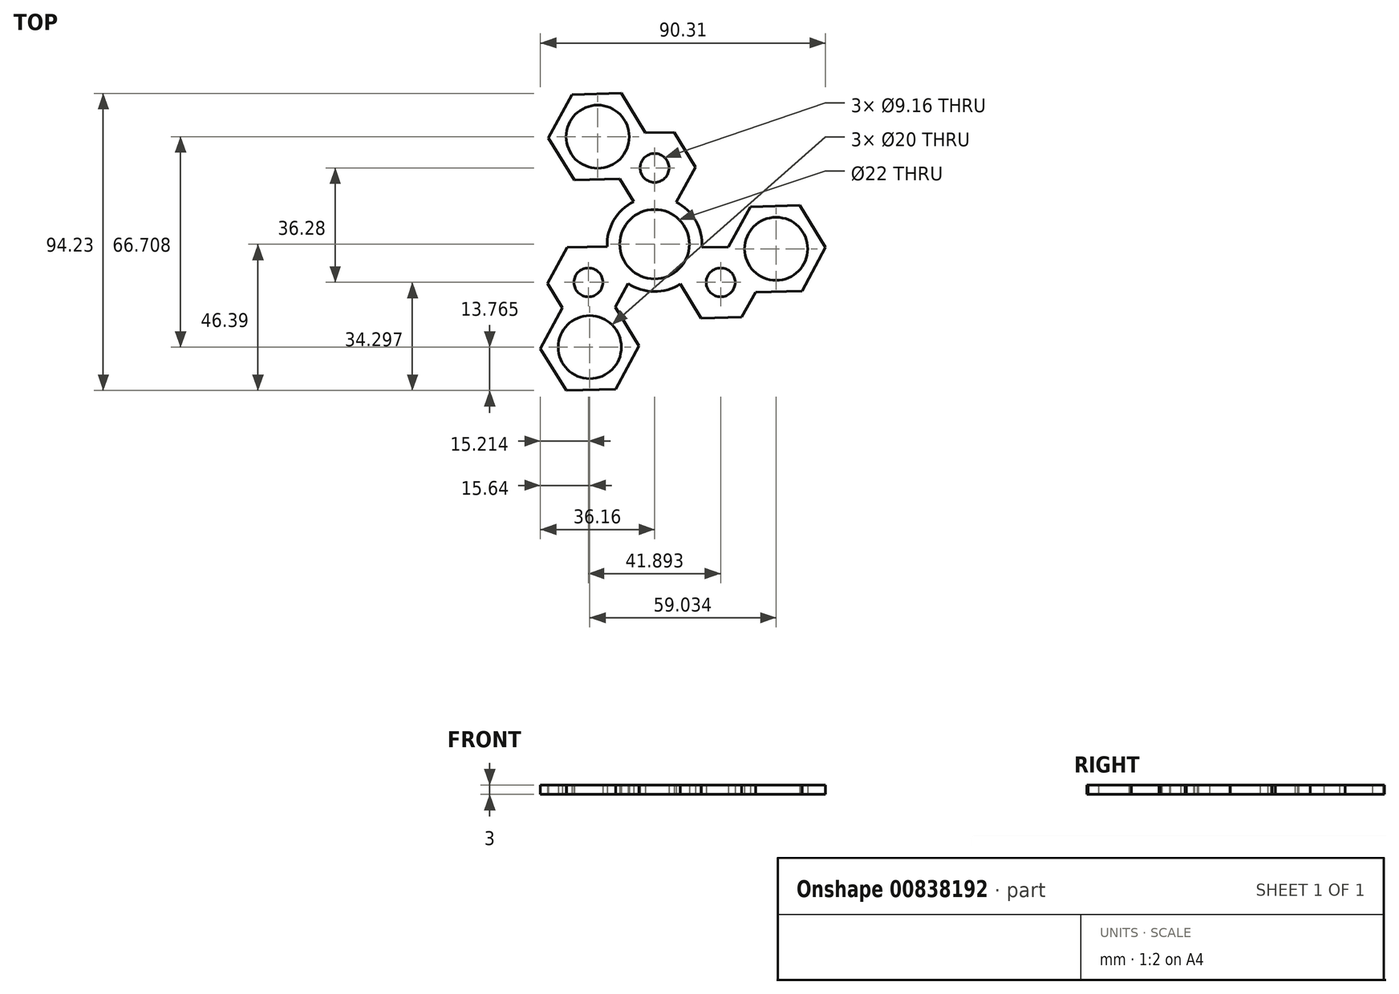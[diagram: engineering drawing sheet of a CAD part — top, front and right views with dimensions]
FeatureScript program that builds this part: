
annotation { "Feature Type Name" : "Feature", "Feature Type Description" : "" }
export const myFeature = defineFeature(function(context is Context, id is Id, definition is map)
    precondition{}
    {
        {
            var Q0;
            Q0=qCreatedBy(makeId("Top.planeOp"),FACE);
            var sketch = newSketch(context, id + "F0", { "sketchPlane" : qUnion([Q0])});
            skCircle(sketch, "E0", {"center": v(0, 0) * mm, "radius": 11 * mm});
            skArc(sketch, "E1", {"start": v(-6.6, 13.47) * mm, "mid": v(-12.93, 7.6) * mm, "end": v(-14.98, -0.78) * mm});
            skLineSegment(sketch, "E2.0", {"start": v(-6.6, 13.47) * mm, "end": v(-10.98, 20.72) * mm});
            skLineSegment(sketch, "E2.2", {"start": v(-2.85, 35.32) * mm, "end": v(6.22, 35.5) * mm});
            skLineSegment(sketch, "E2.3", {"start": v(6.22, 35.5) * mm, "end": v(12.91, 24.45) * mm});
            skLineSegment(sketch, "E2.4", {"start": v(12.91, 24.45) * mm, "end": v(6.81, 13.36) * mm});
            skCircle(sketch, "E3", {"center": v(0, 24.19) * mm, "radius": 4.58 * mm});
            skLineSegment(sketch, "E4.0", {"start": v(-10.98, 20.72) * mm, "end": v(-25.44, 20.32) * mm});
            skLineSegment(sketch, "E4.1", {"start": v(-25.44, 20.32) * mm, "end": v(-33.63, 33.65) * mm});
            skLineSegment(sketch, "E4.2", {"start": v(-33.63, 33.65) * mm, "end": v(-26.19, 47.41) * mm});
            skLineSegment(sketch, "E4.3", {"start": v(-26.19, 47.41) * mm, "end": v(-10.55, 47.84) * mm});
            skLineSegment(sketch, "E4.4", {"start": v(-10.55, 47.84) * mm, "end": v(-2.85, 35.32) * mm});
            skCircle(sketch, "E5", {"center": v(-18, 34.08) * mm, "radius": 10 * mm});
            skCircle(sketch, "E6.1.0", {"center": v(-20.52, -32.63) * mm, "radius": 10 * mm});
            skLineSegment(sketch, "E6.1.1", {"start": v(-27.64, -1.04) * mm, "end": v(-14.98, -0.78) * mm});
            skLineSegment(sketch, "E6.1.2", {"start": v(-8.37, -12.44) * mm, "end": v(-12.46, -19.87) * mm});
            skLineSegment(sketch, "E6.1.3", {"start": v(-29.16, -20.12) * mm, "end": v(-33.86, -12.36) * mm});
            skLineSegment(sketch, "E6.1.4", {"start": v(-12.46, -19.87) * mm, "end": v(-4.88, -32.2) * mm});
            skLineSegment(sketch, "E6.1.5", {"start": v(-4.88, -32.2) * mm, "end": v(-12.33, -45.95) * mm});
            skLineSegment(sketch, "E6.1.6", {"start": v(-27.97, -46.39) * mm, "end": v(-36.16, -33.06) * mm});
            skCircle(sketch, "E6.1.7", {"center": v(-20.95, -12.1) * mm, "radius": 4.58 * mm});
            skLineSegment(sketch, "E6.1.8", {"start": v(-12.33, -45.95) * mm, "end": v(-27.97, -46.39) * mm});
            skLineSegment(sketch, "E6.1.9", {"start": v(-36.16, -33.06) * mm, "end": v(-29.16, -20.12) * mm});
            skLineSegment(sketch, "E6.1.10", {"start": v(-33.86, -12.36) * mm, "end": v(-27.64, -1.04) * mm});
            skCircle(sketch, "E6.2.0", {"center": v(38.51, -1.46) * mm, "radius": 10 * mm});
            skLineSegment(sketch, "E6.2.1", {"start": v(14.72, -23.41) * mm, "end": v(8.17, -12.58) * mm});
            skLineSegment(sketch, "E6.2.2", {"start": v(14.96, -1.03) * mm, "end": v(23.43, -0.85) * mm});
            skLineSegment(sketch, "E6.2.3", {"start": v(32, -15.2) * mm, "end": v(27.64, -23.14) * mm});
            skLineSegment(sketch, "E6.2.4", {"start": v(23.43, -0.85) * mm, "end": v(30.32, 11.87) * mm});
            skLineSegment(sketch, "E6.2.5", {"start": v(30.32, 11.87) * mm, "end": v(45.96, 12.3) * mm});
            skLineSegment(sketch, "E6.2.6", {"start": v(54.15, -1.03) * mm, "end": v(46.7, -14.79) * mm});
            skCircle(sketch, "E6.2.7", {"center": v(20.95, -12.1) * mm, "radius": 4.58 * mm});
            skLineSegment(sketch, "E6.2.8", {"start": v(45.96, 12.3) * mm, "end": v(54.15, -1.03) * mm});
            skLineSegment(sketch, "E6.2.9", {"start": v(46.7, -14.79) * mm, "end": v(32, -15.2) * mm});
            skLineSegment(sketch, "E6.2.10", {"start": v(27.64, -23.14) * mm, "end": v(14.72, -23.41) * mm});
            skArc(sketch, "E7.trimOffspring", {"start": v(-8.37, -12.44) * mm, "mid": v(-0.12, -15) * mm, "end": v(8.17, -12.58) * mm});
            skArc(sketch, "E8.trimOffspring", {"start": v(14.96, -1.03) * mm, "mid": v(13.05, 7.4) * mm, "end": v(6.81, 13.36) * mm});
            skSolve(sketch);
        }
        {
            var Q0;
            Q0 = qSketchRegion(id + "F0", true);
            extrude(context, id + "F1", {"entities" : qUnion([Q0]), "depth" : 3 * mm, "offsetDistance" : 25 * mm});
        }
    });
